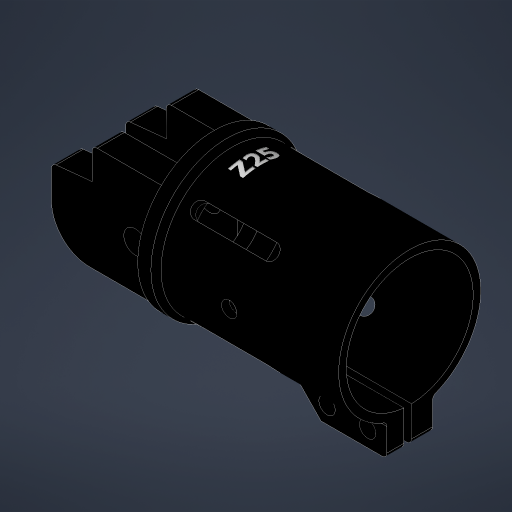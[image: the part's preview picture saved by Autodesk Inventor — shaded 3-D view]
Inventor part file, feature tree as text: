
AUTODESK INVENTOR PART (.ipt)
format: ipt  version: 2025 (Build 290162010, 162A)  size: 543,232 bytes
history: native  units: mm
features: extrude x15, fillet x4, thread x4, sketch x4, plane x3, projected_geometry x2, chamfer x1, other x1, revolve x1, pattern_circular x1, emboss x1
ambient origin geometry x8: Origin, YZ Plane, XZ Plane, XY Plane, X Axis, Y Axis, Z Axis, Center Point
bodies: Solid1 (feature_tree)
feature tree (37):
  extrude  "Extrusion1"  Depth=38.6mm TaperAngle=0.0deg
  extrude  "Extrusion2"  Depth=30.0mm
  chamfer  "Chamfer1"  Distance=36.0mm
  extrude  "Extrusion3"  Depth=25.0mm
  extrude  "Extrusion4"  Depth=14.0mm
  extrude  "Extrusion5"  Depth=14.0mm TaperAngle=0.0deg
  fillet  "Fillet1"  Radius=5.5mm
  extrude  "Extrusion6"  Depth=14.0mm
  extrude  "Extrusion7"  Depth=14.0mm
  extrude  "Extrusion8"  Depth=14.0mm
  fillet  "Fillet2"  Radius=4.0mm
  extrude  "Extrusion10"  Depth=14.0mm TaperAngle=0.0deg
  plane  "Work Plane1"
  other  "Work Axis1"
  revolve  "Revolution1"  [1 undecoded]
  extrude  "Extrusion11"  Depth=14.0mm
  extrude  "Extrusion12"  Depth=14.0mm
  extrude  "Extrusion13"  Depth=14.0mm
  fillet  "Fillet3"  Radius=29.0mm
  fillet  "Fillet4"  Radius=3.0mm
  extrude  "Extrusion14"  Depth=14.0mm
  extrude  "Extrusion15"  Depth=14.0mm
  plane  "Work Plane2"
  extrude  "Extrusion16"  Depth=14.0mm
  pattern_circular  "Circular Pattern1"  [2 undecoded]
  plane  "Work Plane3"
  emboss  "Emboss1"
  thread  "Thread4"  [1 undecoded]
  thread  "Thread5"  [1 undecoded]
  thread  "Thread6"  [1 undecoded]
  thread  "Thread7"  [1 undecoded]
  sketch  "Sketch5"  dims[d0=30.0mm d1=38.6mm d2=0.0mm]
  sketch  "Sketch7"  dims[d3=28.0mm d4=30.0mm d5=36.0mm d6=0.0mm]
  sketch  "Sketch11"  dims[d7=1.0mm d8=2.0mm d9=45.0deg d10=25.0mm]
  projected_geometry  "Projected Loop1"
  projected_geometry  "Projected Loop2"
  sketch  "Sketch18"  dims[d11=36.0mm d12=0.0mm d13=14.0mm d14=36.0mm d15=0.0mm d16=5.5mm d17=9.0mm d18=5.5mm d19=9.0mm d20=4.0mm d21=19.0mm d22=0.0mm d23=1.0mm d27=3.35mm d28=1.5mm d29=9.0mm d30=29.0mm d31=0.0mm d32=3.0mm d33=3.25mm d34=3.8mm d35=3.0mm d36=8.0mm d37=0.0mm d38=0.0mm d39=3.2mm d40=3.2mm d41=4.0mm d42=0.0mm d43=1.0mm d48=5.75mm d49=5.75mm d50=19.0mm d51=0.0mm d52=14.0mm d53=10.0mm d54=10.0mm d55=7.504916mm d56=9.25mm d57=21.0mm d58=5.375mm d59=5.375mm d60=21.0mm d61=22.0mm d62=0.0mm d63=5.5mm d64=8.75mm d65=0.0mm d66=0.0mm d67=4.5mm d68=14.0mm d69=6.2mm d70=14.0mm d71=0.0mm d72=0.0mm d73=7.5mm d74=1.0mm d75=3.0mm d76=3.0mm d77=14.0mm d78=3.5mm d79=5.5mm d80=3.0mm d81=0.0mm d82=17.0mm d83=17.0mm d84=3.0mm d85=0.0mm d86=0.0mm d87=45.0deg d88=17.5mm d89=14.0mm d90=3.0mm d91=0.0mm d92=0.0mm d93=40.0mm d94=360.0deg d96=14.0mm d97=0.1mm d98=0.0mm d105=5.375mm d106=0.0mm d107=5.375mm d108=0.0mm d109=3.25mm d110=4.15mm d111=0.0mm d112=4.15mm d113=0.0mm d46=0.5mm d47=0.872665mm]
note: 7 required parameter values undecoded (feature->parameter linkage not recoverable at this tier; creation-order binding heuristic only, values carry confidence <= 0.55)